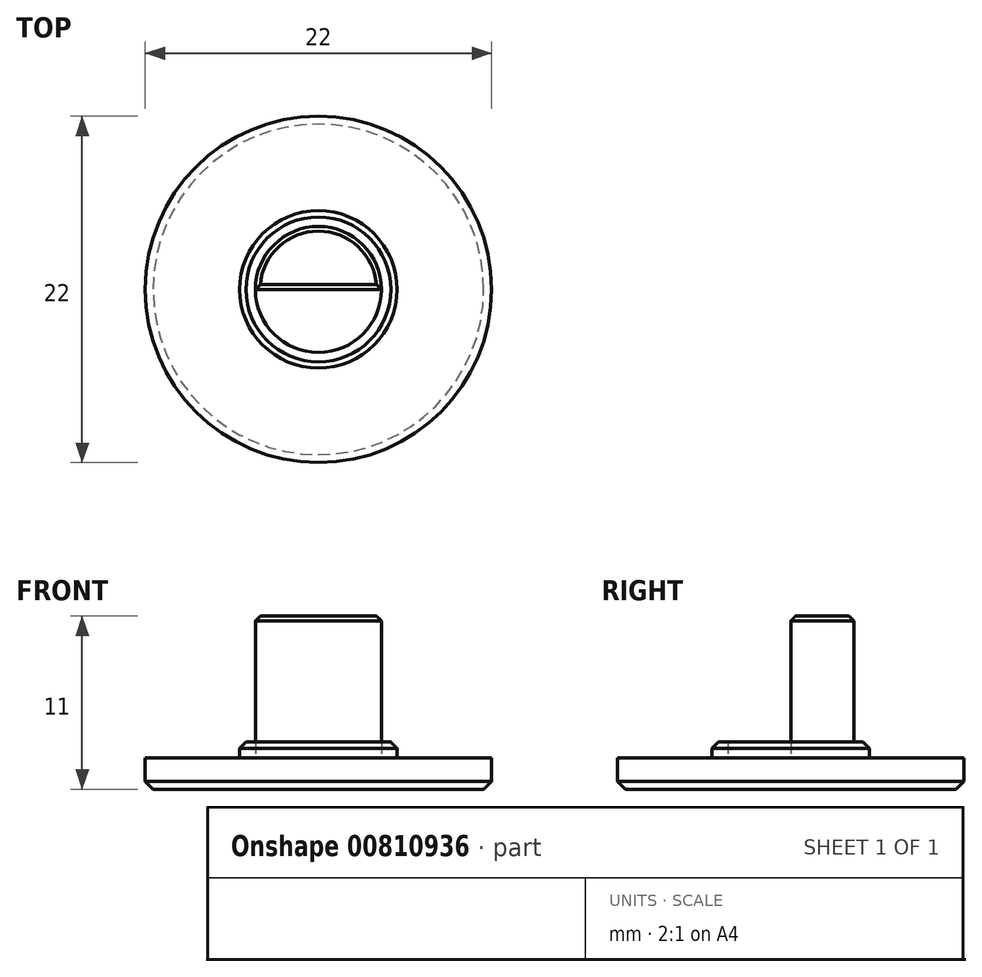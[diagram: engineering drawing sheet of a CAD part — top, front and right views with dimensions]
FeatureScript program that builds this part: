
annotation { "Feature Type Name" : "Feature", "Feature Type Description" : "" }
export const myFeature = defineFeature(function(context is Context, id is Id, definition is map)
    precondition{}
    {
        {
            assignVariable(context, id + "F0", {"name" : "Long", "anyValue" : 11});
        }
        {
            var Q0;
            Q0=qCreatedBy(makeId("Top.planeOp"),FACE);
            var sketch = newSketch(context, id + "F1", { "sketchPlane" : qUnion([Q0])});
            skCircle(sketch, "E0", {"center": v(0, 0) * mm, "radius": 4 * mm});
            skCircle(sketch, "E1", {"center": v(0, 0) * mm, "radius": 5 * mm});
            skCircle(sketch, "E2", {"center": v(0, 0) * mm, "radius": 11 * mm});
            skLineSegment(sketch, "E3", {"start": v(-4, 0) * mm, "end": v(4, 0) * mm});
            skSolve(sketch);
        }
        {
            var Q0;
            {var subQ0=sQuery(id+"F1.wireOp",EDGE,"E3");Q0=makeQuery(id+"F1.imprint","IMPRINT",FACE,{"disambiguationData":[TD([[makeQuery(id+"F1.imprint","IMPRINT",EDGE,{"derivedFrom":subQ0}),1.0]])]});}
            extrude(context, id + "F2", {"entities" : qUnion([Q0]), "depth" : (getVariable(context, 'Long')) * mm, "offsetDistance" : 25 * mm});
        }
        {
            assignVariable(context, id + "F3", {"name" : "Rebord", "anyValue" : 3});
        }
        {
            var Q0;
            Q0=makeQuery(id+"F1.imprint","IMPRINT",FACE,{"disambiguationData":[TD([[makeQuery(id+"F1.imprint","IMPRINT",EDGE,{"derivedFrom":sQuery(id+"F1.wireOp",EDGE,"E1")}),1.0]])]});
            extrude(context, id + "F4", {"entities" : qUnion([Q0]), "operationType" : NewBodyOperationType.ADD, "depth" : (getVariable(context, 'Rebord')) * mm, "offsetDistance" : 25 * mm});
        }
        {
            assignVariable(context, id + "F5", {"name" : "Bouton", "anyValue" : 2});
        }
        {
            var Q0;
            Q0 = qSketchRegion(id + "F1", true);
            extrude(context, id + "F6", {"entities" : qUnion([Q0]), "operationType" : NewBodyOperationType.ADD, "depth" : (getVariable(context, 'Bouton')) * mm, "offsetDistance" : 25 * mm});
        }
        {
            var Q0;
            {var subQ0=sQuery(id+"F1.wireOp",EDGE,"E3");Q0=makeQuery(id+"F1.imprint","IMPRINT",FACE,{"disambiguationData":[TD([[makeQuery(id+"F1.imprint","IMPRINT",EDGE,{"derivedFrom":subQ0}),-1.0]])]});}
            extrude(context, id + "F7", {"entities" : qUnion([Q0]), "operationType" : NewBodyOperationType.ADD, "depth" : 2 * mm, "offsetDistance" : 25 * mm});
        }
        {
            var Q0;
            Q0=makeQuery(id+"F4.opExtrude","CAP_EDGE",EDGE,{"disambiguationData":[OSD([sQuery(id+"F1.wireOp",EDGE,"E1")])],"isStart":false});
            chamfer(context, id + "F8", {"entities" : qUnion([Q0]), "width" : 0.4 * mm, "tangentPropagation" : true});
        }
        {
            var Q0;
            Q0=makeQuery(id+"F2.opExtrude","CAP_EDGE",EDGE,{"disambiguationData":[OSD([sQuery(id+"F1.wireOp",EDGE,"E0")])],"isStart":false});
            var Q1;
            Q1=makeQuery(id+"F2.opExtrude","CAP_EDGE",EDGE,{"disambiguationData":[OSD([sQuery(id+"F1.wireOp",EDGE,"E3")])],"isStart":false});
            chamfer(context, id + "F9", {"entities" : qUnion([Q0, Q1]), "width" : 0.3 * mm, "tangentPropagation" : true});
        }
        {
            var Q0;
            Q0=makeQuery(id+"F6.opExtrude","CAP_EDGE",EDGE,{"disambiguationData":[OSD([sQuery(id+"F1.wireOp",EDGE,"E2")])],"isStart":true});
            chamfer(context, id + "F10", {"entities" : qUnion([Q0]), "width" : 0.5 * mm, "tangentPropagation" : true});
        }
    });
